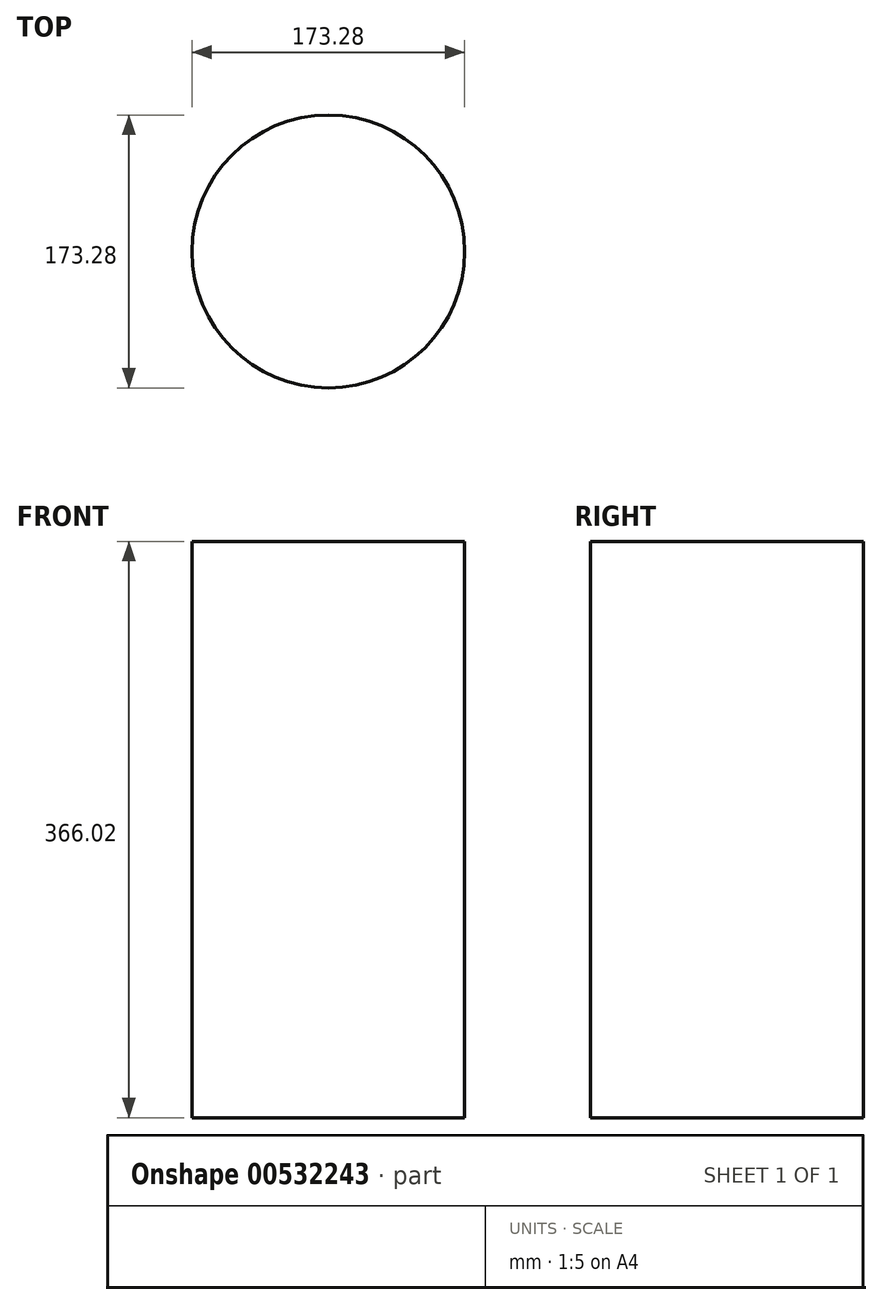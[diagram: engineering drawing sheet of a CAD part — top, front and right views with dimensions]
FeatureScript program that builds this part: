
annotation { "Feature Type Name" : "Feature", "Feature Type Description" : "" }
export const myFeature = defineFeature(function(context is Context, id is Id, definition is map)
    precondition{}
    {
        {
            var Q0;
            Q0=qCreatedBy(makeId("Front.planeOp"),FACE);
            var sketch = newSketch(context, id + "F0", { "sketchPlane" : qUnion([Q0])});
            skLineSegment(sketch, "E0", {"start": v(0, 0) * mm, "end": v(0, -366.02) * mm});
            skLineSegment(sketch, "E1", {"start": v(0, -366.02) * mm, "end": v(86.64, -366.02) * mm});
            skLineSegment(sketch, "E2", {"start": v(86.64, -366.02) * mm, "end": v(86.64, 0) * mm});
            skLineSegment(sketch, "E3", {"start": v(86.64, 0) * mm, "end": v(0, 0) * mm});
            skSolve(sketch);
        }
        {
            var Q0;
            Q0 = qSketchRegion(id + "F0", true);
            var Q1;
            Q1=sQuery(id+"F0.wireOp",EDGE,"E0");
            revolve(context, id + "F1", {"entities" : qUnion([Q0]), "axis" : qUnion([Q1]), "revolveType" : RevolveType.FULL});
        }
    });
